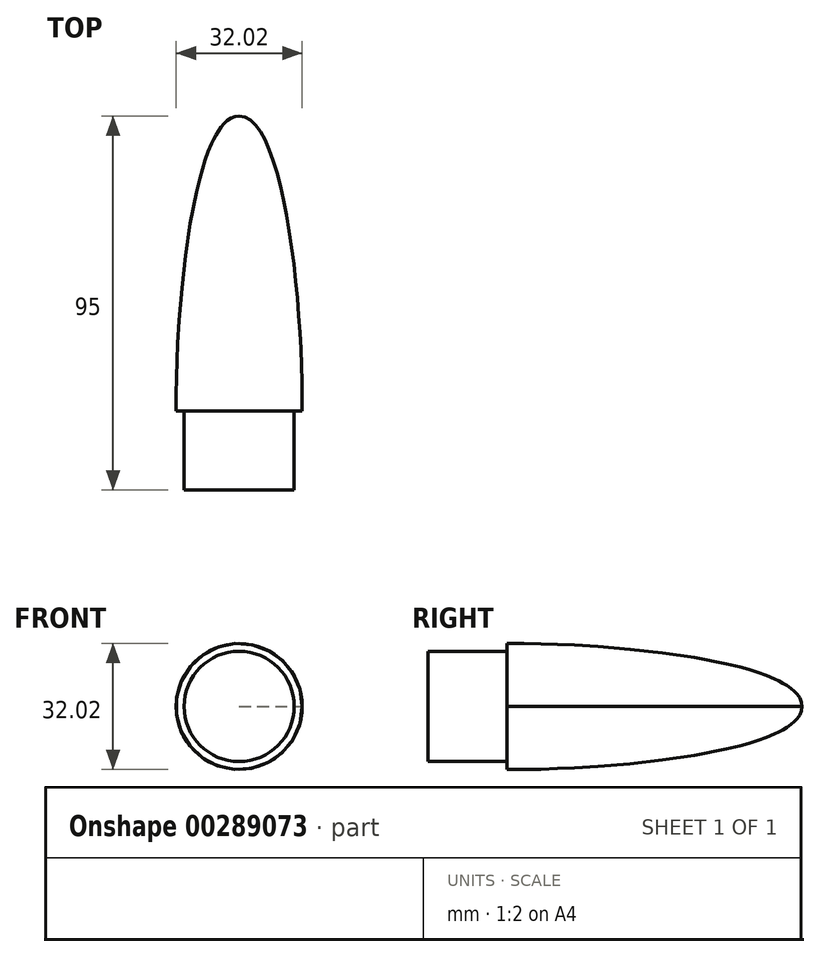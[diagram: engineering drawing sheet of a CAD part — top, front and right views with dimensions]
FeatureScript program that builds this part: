
annotation { "Feature Type Name" : "Feature", "Feature Type Description" : "" }
export const myFeature = defineFeature(function(context is Context, id is Id, definition is map)
    precondition{}
    {
        {
            var Q0;
            Q0=qCreatedBy(makeId("Top.planeOp"),FACE);
            var sketch = newSketch(context, id + "F0", { "sketchPlane" : qUnion([Q0])});
            skLineSegment(sketch, "E0.bottom", {"start": v(-5.5, 65) * mm, "end": v(5.5, 65) * mm});
            skLineSegment(sketch, "E0.top", {"start": v(-5.5, 20) * mm, "end": v(5.5, 20) * mm});
            skLineSegment(sketch, "E0.left", {"start": v(-5.5, 65) * mm, "end": v(-5.5, 20) * mm});
            skLineSegment(sketch, "E0.right", {"start": v(5.5, 65) * mm, "end": v(5.5, 20) * mm});
            skLineSegment(sketch, "E1", {"start": v(0, 0) * mm, "end": v(14, 0) * mm});
            skLineSegment(sketch, "E2", {"start": v(0, 0) * mm, "end": v(-14, 0) * mm});
            skLineSegment(sketch, "E3", {"start": v(-14, 0) * mm, "end": v(-14, 20) * mm});
            skLineSegment(sketch, "E4", {"start": v(-14, 20) * mm, "end": v(14, 20) * mm});
            skLineSegment(sketch, "E5", {"start": v(14, 20) * mm, "end": v(14, 0) * mm});
            skLineSegment(sketch, "E6", {"start": v(-5.5, 20) * mm, "end": v(-5.5, 0) * mm});
            skLineSegment(sketch, "E7", {"start": v(5.5, 20) * mm, "end": v(5.5, 0) * mm});
            skLineSegment(sketch, "E8", {"start": v(14, 20) * mm, "end": v(16, 20) * mm});
            skLineSegment(sketch, "E9", {"start": v(-14, 20) * mm, "end": v(-16, 20) * mm});
            skLineSegment(sketch, "E10", {"start": v(0, 20) * mm, "end": v(0, 95) * mm});
            skFitSpline(sketch, "E11", {"points": [v(0, 95) * mm, v(16, 20) * mm], "startDerivative": vector(34.31, 0.3) * mm, "endDerivative": vector(-0.78, -82.14) * mm});
            skFitSpline(sketch, "E12.MirrorCS", {"points": [v(0, 95) * mm, v(-16, 20) * mm], "startDerivative": vector(-34.31, 0.3) * mm, "endDerivative": vector(0.78, -82.14) * mm});
            skLineSegment(sketch, "E13", {"start": v(0, 20) * mm, "end": v(0, 0) * mm});
            skSolve(sketch);
        }
        {
            var Q0;
            {var subQ1=sQuery(id+"F0.wireOp",EDGE,"E0.right");Q0=makeQuery(id+"F0.imprint","IMPRINT",FACE,{"disambiguationData":[TD([[makeQuery(id+"F0.imprint","IMPRINT",EDGE,{"derivedFrom":subQ1}),1.0]])]});}
            var Q1;
            {var subQ0=sQuery(id+"F0.wireOp",EDGE,"E5");Q1=makeQuery(id+"F0.imprint","IMPRINT",FACE,{"disambiguationData":[TD([[makeQuery(id+"F0.imprint","IMPRINT",EDGE,{"derivedFrom":subQ0}),-1.0]])]});}
            var Q2;
            {var subQ0=sQuery(id+"F0.wireOp",EDGE,"E0.right");Q2=makeQuery(id+"F0.imprint","IMPRINT",FACE,{"disambiguationData":[TD([[makeQuery(id+"F0.imprint","IMPRINT",EDGE,{"derivedFrom":subQ0}),-1.0]])]});}
            var Q3;
            {var subQ2=sQuery(id+"F0.wireOp",EDGE,"E7");Q3=makeQuery(id+"F0.imprint","IMPRINT",FACE,{"disambiguationData":[TD([[makeQuery(id+"F0.imprint","IMPRINT",EDGE,{"derivedFrom":subQ2}),-1.0]])]});}
            var Q4;
            Q4=sQuery(id+"F0.wireOp",EDGE,"E10");
            revolve(context, id + "F1", {"entities" : qUnion([Q0, Q1, Q2, Q3]), "axis" : qUnion([Q4]), "revolveType" : RevolveType.ONE_DIRECTION, "oppositeDirection" : true, "angle" : 360 * degree});
        }
    });
